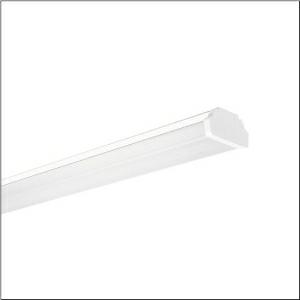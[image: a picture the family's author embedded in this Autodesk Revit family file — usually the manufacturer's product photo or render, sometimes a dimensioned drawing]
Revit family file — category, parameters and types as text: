
# Revit family: dus_r__31_mo_53bd812d2v4085_2fe7
name_source: partatom
category: Lighting Fixtures
units: mm (PartAtom-declared; Revit-internal decimal feet)

## family parameters
Cut with Voids When Loaded = No
Host = Face
Light Source = No
Part Type = Normal
Room Calculation Point = No
Round Connector Dimension = Use Diameter
Shared = No

## types (1)
- --- (1 x LED, 8930 lm, 61.8 W, 4000K)
    Apparent Load = 62 VA
    CIE Flux Codes = 47 80 95 92 100
    Color Rendering = 80
    Color Temperature = 4000K
    Default Elevation = 1800 mm
    Description = DUS® 31 MOluminaire insert, length: 1.535mm, width: 81mm, height: 90mm, LED rated luminous flux: 8.930lm, light colour: 840, control gear: DALI 2, control gear: ECG DALI, with plug, 5-pole, with phase selection, mains connection: 220..240V, AC, 50/60Hz, primary optical cover: cover, of PMMA, light emission: direct distribution, primary light characteristic: symmetric, protection rating (complete): IP20, protection rating (LED compartment): IP50, insulation class (complete): insulation class I (protective earthing), certification: CE, ENEC, VDE, permissible ambient temperature for indoor applications: -25..+30°C, corresponds to IFS (International Featured Standards) requirements for safety and quality in the food industry, reducing of maximum allowable ambient temperature of 5°C with ceiling mounting, packaging unit: 1 piece
    Height = 95 mm
    Lamp = 1 x LED
    Lamp Light Flux = 8930 lm
    Lamp Power = 61.8 W
    Lamp count = 1
    Length = 1535 mm
    Luminous efficacy = 145 lm/W
    Manufacturer = Siteco
    ModVariant = No
    Model = 53BD812D2V4085
    Mounting Place = Ceiling
    Mounting Type = Pendant
    Number of Poles = 1
    OnlyDefault = Yes
    Power Factor = 1
    Product Name = DUS® 31 MO
    Product group = luminaire insert
    ProductGroupID = 902
    Protection Class = Protection class I
    Protection Degree = IP 20
    RLX_Detail_Level = 1
    RlxData = <blob elided: 41777 chars, md5=faf43b23>
    Socket = socket
    Standby Power = 0 W
    System Light Flux = 8930 lm
    System Power = 62 W
    Type Comments = factory setting: luminous flux: 100 % | dim-lin: 254 | 500 mA
    Type Image = l_1003451.jpg
    URL = http://relux.com
    VarID = @adj_117585
    Voltage = 0 V
    Weight = 0.00 kg
    Width = 81 mm

## geometry (parser evidence)
native form markers: Blend x4, Sweep x13
no freeform markers — native parametric forms only
